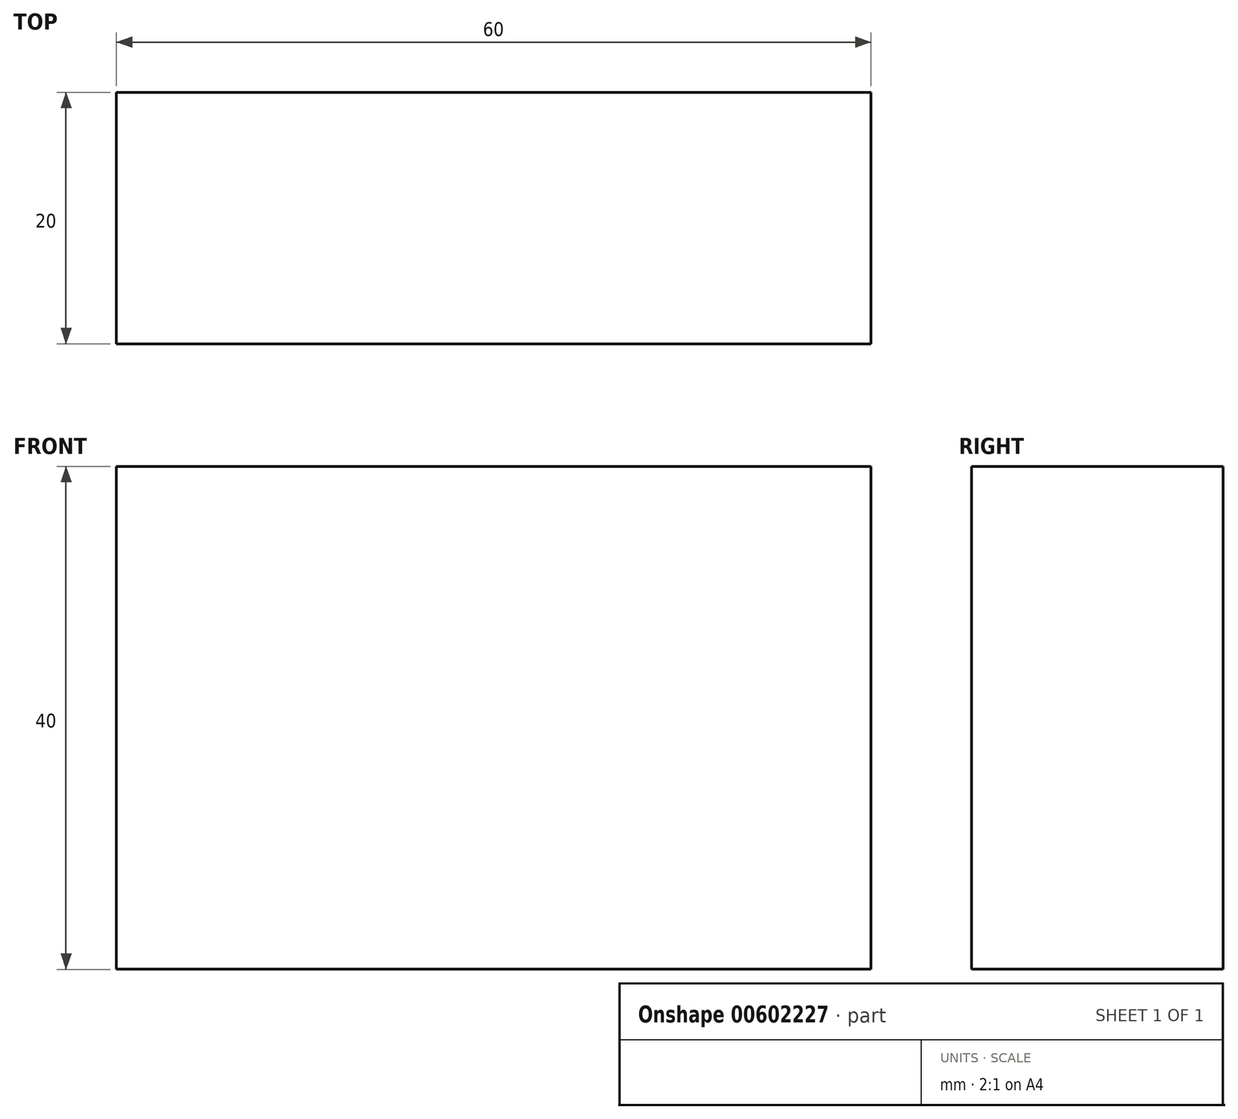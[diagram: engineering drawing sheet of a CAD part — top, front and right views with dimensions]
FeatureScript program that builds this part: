
annotation { "Feature Type Name" : "Feature", "Feature Type Description" : "" }
export const myFeature = defineFeature(function(context is Context, id is Id, definition is map)
    precondition{}
    {
        {
            var Q0;
            Q0=qCreatedBy(makeId("Front.planeOp"),FACE);
            var sketch = newSketch(context, id + "F0", { "sketchPlane" : qUnion([Q0])});
            skLineSegment(sketch, "E0", {"start": v(-44.08, 33.3) * mm, "end": v(15.92, 33.3) * mm});
            skLineSegment(sketch, "E1", {"start": v(15.92, 33.3) * mm, "end": v(15.92, -6.7) * mm});
            skLineSegment(sketch, "E2", {"start": v(15.92, -6.7) * mm, "end": v(-44.08, -6.7) * mm});
            skLineSegment(sketch, "E3", {"start": v(-44.08, -6.7) * mm, "end": v(-44.08, 33.3) * mm});
            skSolve(sketch);
        }
        {
            var Q0;
            Q0 = qSketchRegion(id + "F0", true);
            extrude(context, id + "F1", {"entities" : qUnion([Q0]), "depth" : 20 * mm, "offsetDistance" : 25 * mm});
        }
    });
